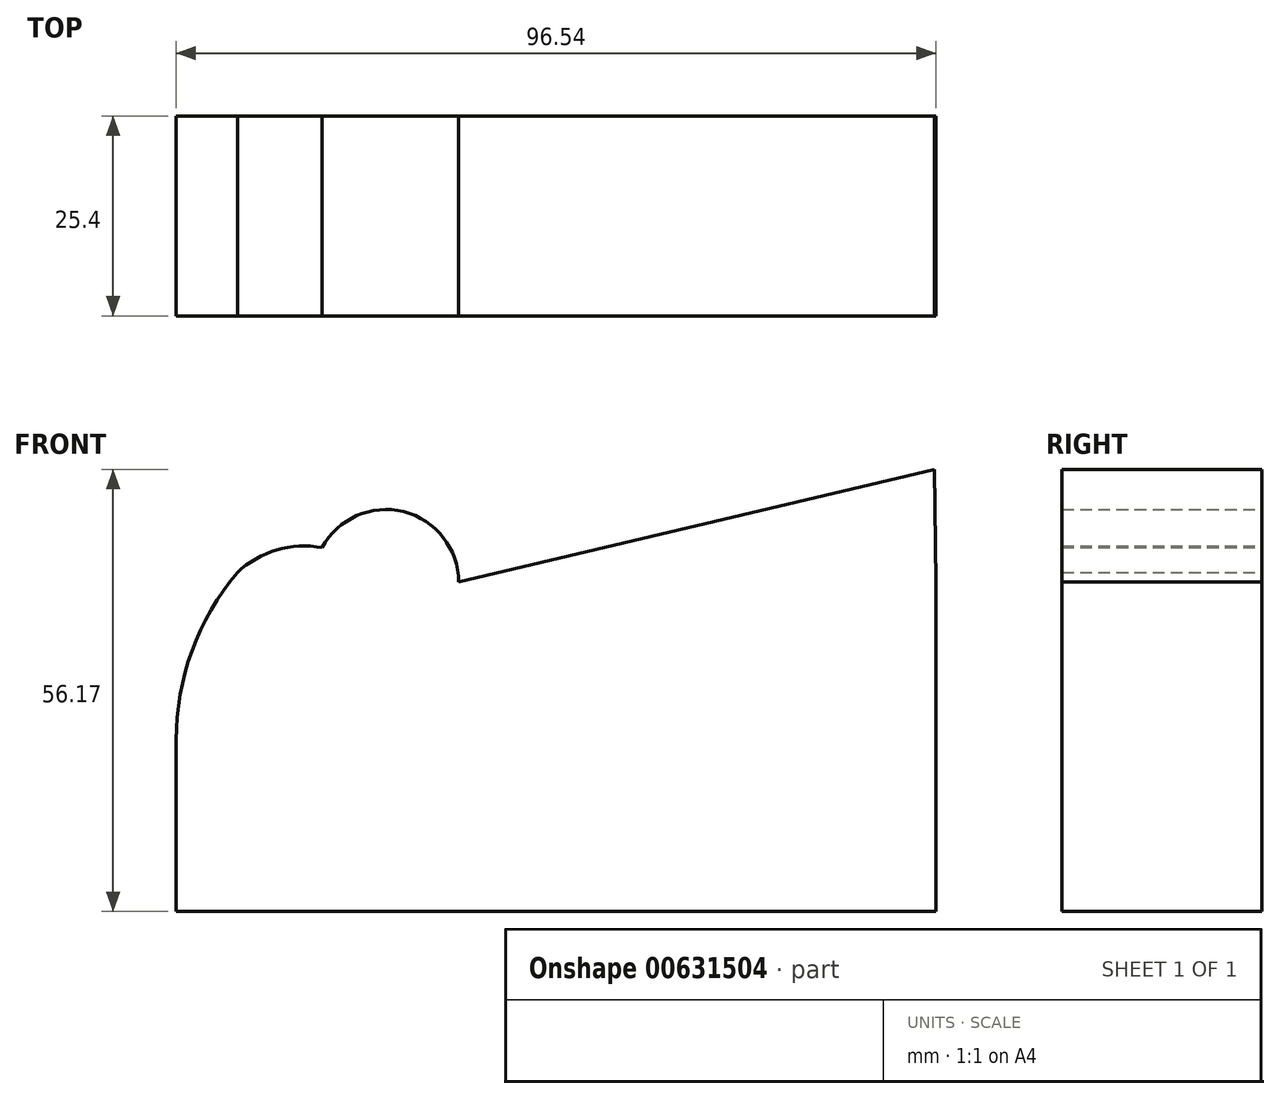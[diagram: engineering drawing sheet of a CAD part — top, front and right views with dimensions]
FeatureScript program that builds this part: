
annotation { "Feature Type Name" : "Feature", "Feature Type Description" : "" }
export const myFeature = defineFeature(function(context is Context, id is Id, definition is map)
    precondition{}
    {
        {
            var Q0;
            Q0=qCreatedBy(makeId("Front.planeOp"),FACE);
            var sketch = newSketch(context, id + "F0", { "sketchPlane" : qUnion([Q0])});
            skLineSegment(sketch, "E0.bottom", {"start": v(-18.69, 10.9) * mm, "end": v(-54.57, 10.9) * mm});
            skLineSegment(sketch, "E0.top", {"start": v(-18.69, -10.9) * mm, "end": v(-54.57, -10.9) * mm});
            skLineSegment(sketch, "E0.left", {"start": v(-18.69, 10.9) * mm, "end": v(-18.69, -10.9) * mm});
            skLineSegment(sketch, "E0.right", {"start": v(-54.57, 10.9) * mm, "end": v(-54.57, -10.9) * mm});
            skPoint(sketch, "E0.middle", {"position": v(-36.63, 0) * mm});
            skLineSegment(sketch, "E1.bottom", {"start": v(-18.69, -10.9) * mm, "end": v(41.97, -10.9) * mm});
            skLineSegment(sketch, "E1.top", {"start": v(-18.69, 30.97) * mm, "end": v(41.97, 30.97) * mm});
            skLineSegment(sketch, "E1.left", {"start": v(-18.69, -10.9) * mm, "end": v(-18.69, 30.97) * mm});
            skLineSegment(sketch, "E1.right", {"start": v(41.97, -10.9) * mm, "end": v(41.97, 30.97) * mm});
            skCircle(sketch, "E2", {"center": v(-38.33, 23.28) * mm, "radius": 12.27 * mm});
            skArc(sketch, "E3", {"start": v(-18.69, 30.97) * mm, "mid": v(-25.66, 39.9) * mm, "end": v(-36.03, 35.33) * mm});
            skArc(sketch, "E4", {"start": v(-54.57, 10.9) * mm, "mid": v(-52.56, 22.22) * mm, "end": v(-46.79, 32.17) * mm});
            skLineSegment(sketch, "E5", {"start": v(-18.69, 30.97) * mm, "end": v(41.75, 45.28) * mm});
            skLineSegment(sketch, "E6", {"start": v(41.97, 30.97) * mm, "end": v(41.75, 45.28) * mm});
            skLineSegment(sketch, "E7", {"start": v(-18.69, 30.97) * mm, "end": v(41.97, -10.9) * mm});
            skLineSegment(sketch, "E8", {"start": v(0, 0) * mm, "end": v(41.97, 30.97) * mm});
            skLineSegment(sketch, "E9", {"start": v(0, 0) * mm, "end": v(0, -10.9) * mm});
            skLineSegment(sketch, "E10", {"start": v(0, 0) * mm, "end": v(-18.69, 30.97) * mm});
            skSolve(sketch);
        }
        {
            var Q0;
            Q0=makeQuery(id+"F0.imprint","IMPRINT",FACE,{"disambiguationData":[TD([[makeQuery(id+"F0.imprint","IMPRINT",EDGE,{"derivedFrom":sQuery(id+"F0.wireOp",EDGE,"E1.top")}),1.0]])]});
            var Q1;
            {var subQ0=sQuery(id+"F0.wireOp",EDGE,"E4");var subQ1=sQuery(id+"F0.wireOp",EDGE,"E2");var subQ2=makeQuery(id+"F0.imprint","INTERSECT",VERTEX,{"disambiguationData":[OD(0.0)],"derivedFrom":[subQ1,subQ0]});Q1=makeQuery(id+"F0.imprint","IMPRINT",FACE,{"disambiguationData":[TD([[makeQuery(id+"F0.imprint","IMPRINT",EDGE,{"disambiguationData":[TD([[subQ2,-1.0]])],"derivedFrom":subQ1}),1.0]])]});}
            var Q2;
            {var subQ0=sQuery(id+"F0.wireOp",EDGE,"E0.bottom");Q2=makeQuery(id+"F0.imprint","IMPRINT",FACE,{"disambiguationData":[TD([[makeQuery(id+"F0.imprint","IMPRINT",EDGE,{"derivedFrom":subQ0}),1.0]])]});}
            var Q3;
            {var subQ0=sQuery(id+"F0.wireOp",EDGE,"E1.right");Q3=makeQuery(id+"F0.imprint","IMPRINT",FACE,{"disambiguationData":[TD([[makeQuery(id+"F0.imprint","IMPRINT",EDGE,{"derivedFrom":subQ0}),1.0]])]});}
            var Q4;
            {var subQ4=sQuery(id+"F0.wireOp",EDGE,"E0.bottom");Q4=makeQuery(id+"F0.imprint","IMPRINT",FACE,{"disambiguationData":[TD([[makeQuery(id+"F0.imprint","IMPRINT",EDGE,{"derivedFrom":subQ4}),-1.0]])]});}
            var Q5;
            {var subQ3=sQuery(id+"F0.wireOp",EDGE,"E9");Q5=makeQuery(id+"F0.imprint","IMPRINT",FACE,{"disambiguationData":[TD([[makeQuery(id+"F0.imprint","IMPRINT",EDGE,{"derivedFrom":subQ3}),1.0]])]});}
            var Q6;
            {var subQ0=sQuery(id+"F0.wireOp",EDGE,"E1.top");Q6=makeQuery(id+"F0.imprint","IMPRINT",FACE,{"disambiguationData":[TD([[makeQuery(id+"F0.imprint","IMPRINT",EDGE,{"derivedFrom":subQ0}),-1.0]])]});}
            var Q7;
            {var subQ0=sQuery(id+"F0.wireOp",EDGE,"E10");Q7=makeQuery(id+"F0.imprint","IMPRINT",FACE,{"disambiguationData":[TD([[makeQuery(id+"F0.imprint","IMPRINT",EDGE,{"derivedFrom":subQ0}),-1.0]])]});}
            var Q8;
            {var subQ3=sQuery(id+"F0.wireOp",EDGE,"E9");Q8=makeQuery(id+"F0.imprint","IMPRINT",FACE,{"disambiguationData":[TD([[makeQuery(id+"F0.imprint","IMPRINT",EDGE,{"derivedFrom":subQ3}),-1.0]])]});}
            extrude(context, id + "F1", {"entities" : qUnion([Q0, Q1, Q2, Q3, Q4, Q5, Q6, Q7, Q8]), "depth" : 25.4 * mm, "offsetDistance" : 25.4 * mm});
        }
    });
